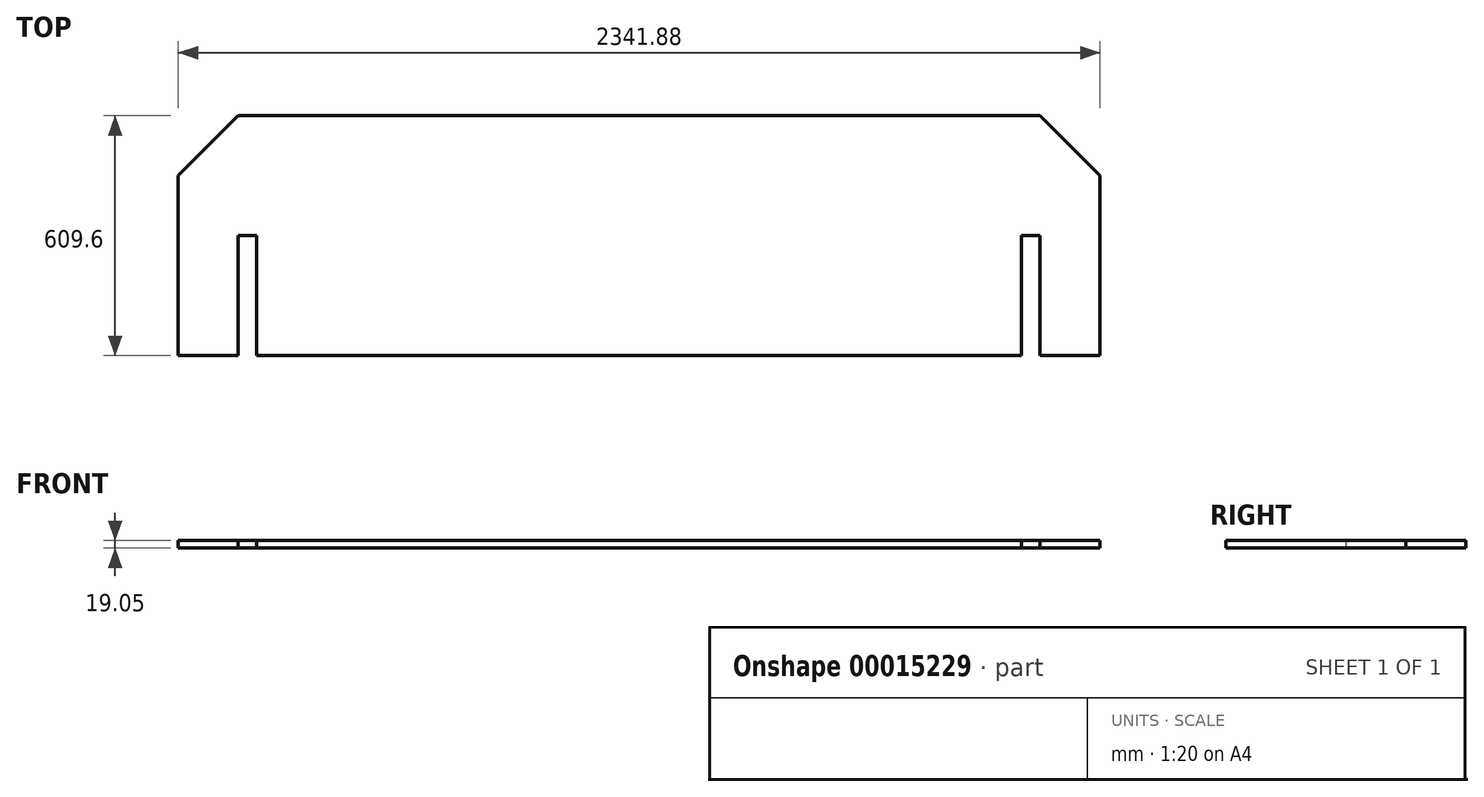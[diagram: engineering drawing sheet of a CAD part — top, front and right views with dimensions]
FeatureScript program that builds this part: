
annotation { "Feature Type Name" : "Feature", "Feature Type Description" : "" }
export const myFeature = defineFeature(function(context is Context, id is Id, definition is map)
    precondition{}
    {
        {
            var Q0;
            Q0=qCreatedBy(makeId("Top.planeOp"),FACE);
            var sketch = newSketch(context, id + "F0", { "sketchPlane" : qUnion([Q0])});
            skLineSegment(sketch, "E0.bottom", {"start": v(-1083.43, 347.63) * mm, "end": v(953.65, 347.63) * mm});
            skLineSegment(sketch, "E0.top", {"start": v(-1235.83, -261.97) * mm, "end": v(-1083.43, -261.97) * mm});
            skLineSegment(sketch, "E0.left", {"start": v(-1235.83, 347.63) * mm, "end": v(-1235.83, -261.97) * mm});
            skLineSegment(sketch, "E0.right", {"start": v(1106.05, 347.63) * mm, "end": v(1106.05, -261.97) * mm});
            skLineSegment(sketch, "E1", {"start": v(-1083.43, 347.63) * mm, "end": v(-1235.83, 195.23) * mm});
            skLineSegment(sketch, "E2", {"start": v(953.65, 347.63) * mm, "end": v(1106.05, 195.23) * mm});
            skPoint(sketch, "E3.top.end.orphan", {"position": v(953.65, 42.83) * mm});
            skPoint(sketch, "E3.top.start.orphan", {"position": v(1001.91, 42.83) * mm});
            skLineSegment(sketch, "E4.bottom", {"start": v(906.66, 42.83) * mm, "end": v(953.65, 42.83) * mm});
            skLineSegment(sketch, "E4.left", {"start": v(906.66, 42.83) * mm, "end": v(906.66, -261.97) * mm});
            skLineSegment(sketch, "E4.right", {"start": v(953.65, 42.83) * mm, "end": v(953.65, -261.97) * mm});
            skLineSegment(sketch, "E5.trimOffspring", {"start": v(953.65, -261.97) * mm, "end": v(1106.05, -261.97) * mm});
            skLineSegment(sketch, "E6.top", {"start": v(-1083.43, 42.83) * mm, "end": v(-1036.44, 42.83) * mm});
            skLineSegment(sketch, "E6.left", {"start": v(-1083.43, -261.97) * mm, "end": v(-1083.43, 42.83) * mm});
            skLineSegment(sketch, "E6.right", {"start": v(-1036.44, -261.97) * mm, "end": v(-1036.44, 42.83) * mm});
            skLineSegment(sketch, "E7.trimOffspring", {"start": v(-1036.44, -261.97) * mm, "end": v(906.66, -261.97) * mm});
            skSolve(sketch);
        }
        {
            var Q0;
            Q0 = qSketchRegion(id + "F0", true);
            extrude(context, id + "F1", {"entities" : qUnion([Q0]), "depth" : 19.05 * mm});
        }
    });
